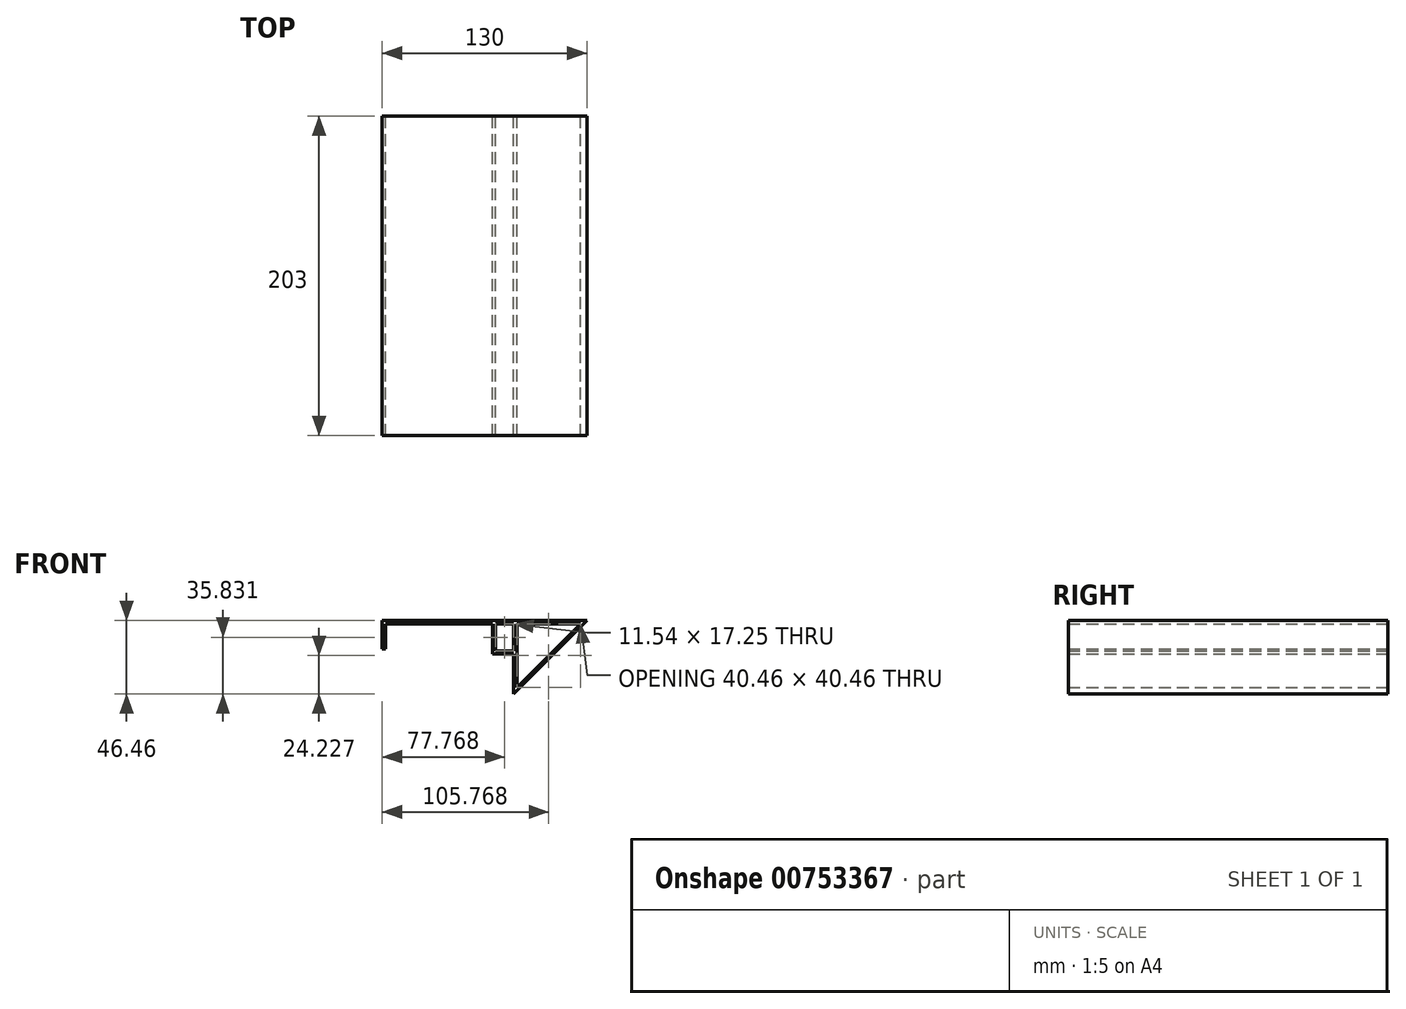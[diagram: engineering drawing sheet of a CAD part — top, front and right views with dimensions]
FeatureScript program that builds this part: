
annotation { "Feature Type Name" : "Feature", "Feature Type Description" : "" }
export const myFeature = defineFeature(function(context is Context, id is Id, definition is map)
    precondition{}
    {
        {
            var Q0;
            Q0=qCreatedBy(makeId("Front.planeOp"),FACE);
            var sketch = newSketch(context, id + "F0", { "sketchPlane" : qUnion([Q0])});
            skPoint(sketch, "E0", {"position": v(-33.48, 21.1) * mm});
            skPoint(sketch, "E1", {"position": v(-101.48, 21.1) * mm});
            skLineSegment(sketch, "E2", {"start": v(-101.48, 21.1) * mm, "end": v(-33.48, 21.1) * mm});
            skLineSegment(sketch, "E3", {"start": v(-101.48, 21.1) * mm, "end": v(-101.48, 5.1) * mm});
            skLineSegment(sketch, "E4", {"start": v(-101.48, 5.1) * mm, "end": v(-103.48, 5.1) * mm});
            skPoint(sketch, "E5", {"position": v(-103.48, 5.1) * mm});
            skLineSegment(sketch, "E6", {"start": v(-103.48, 5.1) * mm, "end": v(-103.48, 21.1) * mm});
            skLineSegment(sketch, "E7", {"start": v(-103.48, 21.1) * mm, "end": v(-103.48, 23.1) * mm});
            skLineSegment(sketch, "E8", {"start": v(-103.48, 23.1) * mm, "end": v(26.52, 23.1) * mm});
            skLineSegment(sketch, "E9", {"start": v(-33.48, 21.1) * mm, "end": v(-33.48, 1.86) * mm});
            skLineSegment(sketch, "E10", {"start": v(26.52, 23.1) * mm, "end": v(-14.52, -17.93) * mm});
            skLineSegment(sketch, "E11", {"start": v(-14.52, -17.93) * mm, "end": v(-19.94, -23.35) * mm});
            skLineSegment(sketch, "E12", {"start": v(-33.48, 1.86) * mm, "end": v(-19.94, 1.86) * mm});
            skLineSegment(sketch, "E13", {"start": v(-19.94, 1.86) * mm, "end": v(-19.94, -23.35) * mm});
            skLineSegment(sketch, "E14", {"start": v(-19.94, 1.86) * mm, "end": v(-19.94, 23.1) * mm});
            skPoint(sketch, "E15", {"position": v(-31.48, 1.86) * mm});
            skPoint(sketch, "E16", {"position": v(-21.94, 1.86) * mm});
            skLineSegment(sketch, "E17", {"start": v(-31.48, 1.86) * mm, "end": v(-31.48, 23.1) * mm});
            skPoint(sketch, "E18", {"position": v(-19.94, 3.86) * mm});
            skLineSegment(sketch, "E19", {"start": v(-19.94, 3.86) * mm, "end": v(-33.48, 3.86) * mm});
            skPoint(sketch, "E20", {"position": v(-17.94, 23.1) * mm});
            skPoint(sketch, "E21", {"position": v(24.52, 23.1) * mm});
            skLineSegment(sketch, "E22", {"start": v(24.52, 23.1) * mm, "end": v(-19.94, -21.35) * mm});
            skLineSegment(sketch, "E23", {"start": v(-17.94, 23.1) * mm, "end": v(-17.94, -19.35) * mm});
            skLineSegment(sketch, "E24", {"start": v(-33.48, 21.1) * mm, "end": v(24.52, 21.1) * mm});
            skSolve(sketch);
        }
        {
            var Q0;
            Q0=qSketchRegion(id+"F0",true);
            extrude(context, id + "F1", {"entities" : qUnion([Q0]), "depth" : 203 * mm, "offsetDistance" : 25 * mm});
        }
    });
